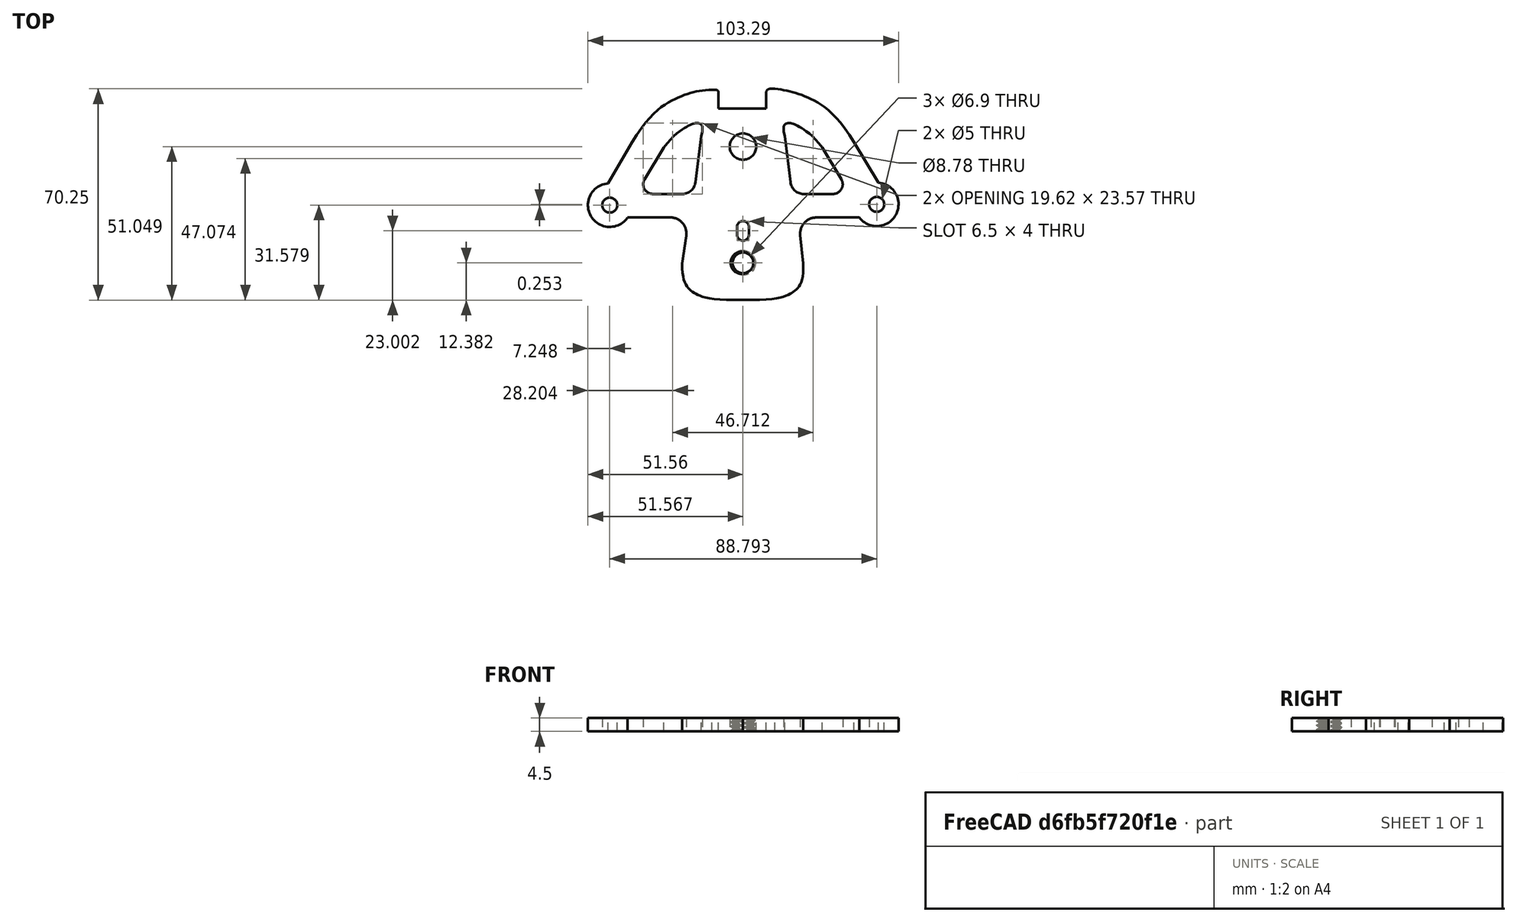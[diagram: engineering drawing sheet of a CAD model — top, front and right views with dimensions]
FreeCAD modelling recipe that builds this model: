
FCSTD DOCUMENT  (FreeCAD 0.20R29603 (Git))
Label: tiller-plate-final-threaded
License: Creative Commons Attribution
LicenseURL: http://creativecommons.org/licenses/by/4.0/
objects: Sketcher::SketchObject×2, Image::ImagePlane×1, PartDesign::Pad×1, PartDesign::Hole×1, PartDesign::Body×1, Part::Refine×1, Mesh::Feature×1
note: 8 computed .brp shape members not serialized (recipe doc carries the construction recipe); baked Part::Feature solids carry a one-line shape summary decoded from their .brp

FEATURE [Image::ImagePlane] ImagePlane
  Placement = pos=(0.718471,-0.887185,-0.1) rot=(0,0,-1;6.26573rad)
  XSize = 116.42
  YSize = 72.9857
FEATURE [Sketcher::SketchObject] Sketch
  FullyConstrained = false
  MapMode = 5
  Support = -> [XY_Plane]
  sketch-geometry (75):
    g0: ArcOfCircle CenterX=-44.3115 CenterY=-4.63128 CenterZ=0 NormalX=0 NormalY=0 NormalZ=1 AngleXU=0 Radius=7.25 StartAngle=1.65486 EndAngle=5.682
    g1: LineSegment StartX=-8.13082 StartY=27.4789 StartZ=0 EndX=7.6791 EndY=27.4789 EndZ=0
    g2: ArcOfCircle CenterX=44.4815 CenterY=-4.37835 CenterZ=0 NormalX=0 NormalY=0 NormalZ=1 AngleXU=0 Radius=7.25 StartAngle=3.79043 EndAngle=7.77353
    g3-g7: Circle x5 (B-spline internal-alignment scaffolding for g8; pole/knot coordinates omitted)
    g8: BSplineCurve PolesCount=5 KnotsCount=3 Degree=3 IsPeriodic=0
    g9: GeomPoint X=-36.8504 Y=16.2655 Z=0
    g10: GeomPoint X=-22.0365 Y=30.9294 Z=0
    g11: GeomPoint X=-10.281 Y=33.7257 Z=0
    g12: LineSegment StartX=-8.13082 StartY=27.4789 StartZ=0 EndX=-8.13082 EndY=32.8031 EndZ=0
    g13: LineSegment StartX=-10.281 StartY=33.7257 StartZ=0 EndX=-9.05342 EndY=33.7257 EndZ=0
    g14: ArcOfCircle CenterX=-9.05342 CenterY=32.8031 CenterZ=0 NormalX=0 NormalY=0 NormalZ=1 AngleXU=0 Radius=0.922601 StartAngle=2.8e-15 EndAngle=1.5708
    g15: LineSegment StartX=-44.9203 StartY=2.59312 StartZ=0 EndX=-36.8504 EndY=16.2655 EndZ=0
    g16: LineSegment StartX=45.0641 StartY=2.84821 StartZ=0 EndX=36.8504 EndY=16.2655 EndZ=0
    g17: BSplineCurve PolesCount=5 KnotsCount=3 Degree=3 IsPeriodic=0
    g18: Circle CenterX=10.5661 CenterY=34.0385 CenterZ=0 NormalX=0 NormalY=0 NormalZ=1 AngleXU=0 Radius=1
    g19: GeomPoint X=10.5661 Y=34.0385 Z=0
    g20: LineSegment StartX=7.6791 StartY=27.4789 StartZ=0 EndX=7.6791 EndY=32.7332 EndZ=0
    g21: LineSegment StartX=10.5661 StartY=34.0385 StartZ=0 EndX=8.9844 EndY=34.0385 EndZ=0
    g22: ArcOfCircle CenterX=8.9844 CenterY=32.7332 CenterZ=0 NormalX=0 NormalY=0 NormalZ=1 AngleXU=0 Radius=1.3053 StartAngle=1.5708 EndAngle=3.14159
    g23: Circle CenterX=0 CenterY=14.839 CenterZ=0 NormalX=0 NormalY=0 NormalZ=1 AngleXU=0 Radius=4.39
    g24: Circle CenterX=-44.3115 CenterY=-4.63128 CenterZ=0 NormalX=0 NormalY=0 NormalZ=1 AngleXU=0 Radius=2.5
    g25: Circle CenterX=44.4815 CenterY=-4.37835 CenterZ=0 NormalX=0 NormalY=0 NormalZ=1 AngleXU=0 Radius=2.5
    g26: Circle CenterX=0 CenterY=-23.8283 CenterZ=0 NormalX=0 NormalY=0 NormalZ=1 AngleXU=0 Radius=3.375
    g27: LineSegment StartX=-24.1418 StartY=-8.73204 StartZ=0 EndX=-38.3327 EndY=-8.73204 EndZ=0
    g28: LineSegment StartX=-18.8831 StartY=-14.7976 StartZ=0 EndX=-20.2109 EndY=-24.0676 EndZ=0
    g29: ArcOfCircle CenterX=-24.1418 CenterY=-14.0444 CenterZ=0 NormalX=0 NormalY=0 NormalZ=1 AngleXU=0 Radius=5.31234 StartAngle=6.14092 EndAngle=7.85398
    g30: LineSegment StartX=24.3717 StartY=-8.75921 StartZ=0 EndX=38.7048 EndY=-8.75921 EndZ=0
    g31: ArcOfCircle CenterX=24.3717 CenterY=-14.1062 CenterZ=0 NormalX=0 NormalY=0 NormalZ=1 AngleXU=0 Radius=5.34701 StartAngle=1.5708 EndAngle=3.24394
    g32: LineSegment StartX=19.0527 StartY=-14.6525 StartZ=0 EndX=20.0104 EndY=-23.9781 EndZ=0
    g33: LineSegment StartX=-1.99308 StartY=-11.9579 StartZ=0 EndX=-1.99308 EndY=-14.4579 EndZ=0
    g34: ArcOfCircle CenterX=0.00691514 CenterY=-14.4579 CenterZ=0 NormalX=0 NormalY=0 NormalZ=1 AngleXU=0 Radius=2 StartAngle=3.14159 EndAngle=6.28319
    g35: LineSegment StartX=2.00692 StartY=-14.4579 StartZ=0 EndX=2.00692 EndY=-11.9579 EndZ=0
    g36: ArcOfCircle CenterX=0.00691514 CenterY=-11.9579 CenterZ=0 NormalX=0 NormalY=0 NormalZ=1 AngleXU=0 Radius=2 StartAngle=0 EndAngle=3.14159
    g37-g41: Circle x5 (B-spline internal-alignment scaffolding for g42; pole/knot coordinates omitted)
    g42: BSplineCurve PolesCount=5 KnotsCount=3 Degree=3 IsPeriodic=0
    g43: GeomPoint X=-20.2109 Y=-24.0676 Z=0
    g44: GeomPoint X=-16.4959 Y=-33.6189 Z=0
    g45: GeomPoint X=0 Y=-36.2033 Z=0
    g46: BSplineCurve PolesCount=5 KnotsCount=3 Degree=3 IsPeriodic=0
    g47: LineSegment StartX=-13.8688 StartY=18.3787 StartZ=0 EndX=-15.7977 EndY=2.95357 EndZ=0
    g48: LineSegment StartX=-29.9555 StartY=-0.921458 StartZ=0 EndX=-20.1874 EndY=-0.921458 EndZ=0
    g49: ArcOfCircle CenterX=-20.1874 CenterY=3.50249 CenterZ=0 NormalX=0 NormalY=0 NormalZ=1 AngleXU=0 Radius=4.42394 StartAngle=4.71239 EndAngle=6.15879
    g50: LineSegment StartX=-26.3153 StartY=14.4759 StartZ=0 EndX=-32.7012 EndY=3.9578 EndZ=0
    g51: ArcOfCircle CenterX=-29.9555 CenterY=2.29074 CenterZ=0 NormalX=0 NormalY=0 NormalZ=1 AngleXU=0 Radius=3.2122 StartAngle=2.59594 EndAngle=4.71239
    g52-g57: Circle x6 (B-spline internal-alignment scaffolding for g58; pole/knot coordinates omitted)
    g58: BSplineCurve PolesCount=6 KnotsCount=4 Degree=3 IsPeriodic=0
    g59-g62: GeomPoint x4 (B-spline internal-alignment scaffolding for g58; pole/knot coordinates omitted)
    g63: GeomPoint X=0 Y=-23.8283 Z=0
    g64: LineSegment StartX=26.3153 StartY=14.4759 StartZ=0 EndX=32.7012 EndY=3.9578 EndZ=0
    g65: BSplineCurve PolesCount=6 KnotsCount=4 Degree=3 IsPeriodic=0
    g66: LineSegment StartX=13.8688 StartY=18.3787 StartZ=0 EndX=15.7977 EndY=2.95357 EndZ=0
    g67: ArcOfCircle CenterX=20.1874 CenterY=3.50249 CenterZ=0 NormalX=0 NormalY=0 NormalZ=1 AngleXU=0 Radius=4.42394 StartAngle=3.26599 EndAngle=4.71239
    g68: LineSegment StartX=29.9555 StartY=-0.921458 StartZ=0 EndX=20.1874 EndY=-0.921458 EndZ=0
    g69: ArcOfCircle CenterX=29.9555 CenterY=2.29074 CenterZ=0 NormalX=0 NormalY=0 NormalZ=1 AngleXU=0 Radius=3.2122 StartAngle=4.71239 EndAngle=6.82884
    g70: GeomPoint X=-0.103427 Y=-16.4548 Z=0
    g71: GeomPoint X=-0.101997 Y=-20.4548 Z=0
    g72: GeomPoint X=0.0131789 Y=-27.2033 Z=0
    g73: GeomPoint X=-0.00257 Y=27.4789 Z=0
    g74: GeomPoint X=-0.0300529 Y=19.2289 Z=0
  constraints (86):
    c: Radius(g0) = 7.25
    c: Horizontal(g1)
    c: Equal(g2,g0)
    c: Equal(g3, g4-g7) x4
    c: InternalAlignment(g3-g7 -> g8) x5
    c: InternalAlignment(g9,g8)
    c: InternalAlignment(g10,g8)
    c: InternalAlignment(g11,g8)
    c: Coincident(g12,g1)
    c: Coincident(g13,g8)
    c: Horizontal(g13)
    c: Tangent(g12,g14) = -1.5708
    c: Tangent(g13,g14) = 1.5708
    c: Coincident(g15,g8)
    c: InternalAlignment(g18,g17)
    c: InternalAlignment(g19,g17)
    c: Coincident(g21,g17)
    c: Horizontal(g21)
    c: Tangent(g20,g22) = 1.5708
    c: Tangent(g21,g22) = -1.5708
    c: Coincident(g16,g17)
    c: PointOnObject(g23,g-2)
    c: Coincident(g24,g0)
    c: Diameter(g24) = 5
    c: Diameter(g25) = 5
    c: PointOnObject(g26,g-2)
    c: Horizontal(g27)
    c: Tangent(g27,g29) = -1.5708
    c: Tangent(g28,g29) = 1.5708
    c: Horizontal(g30)
    c: Tangent(g30,g31) = 1.5708
    c: Tangent(g32,g31) = -1.5708
    c: Coincident(g2,g25)
    c: Vertical(g33)
    c: Tangent(g33,g34) = -1.5708
    c: Tangent(g34,g35) = -1.5708
    c: Tangent(g35,g36) = -1.5708
    c: Radius(g36) = 2
    c: Equal(g34,g36)
    c: DistanceY(g34,g36) = 2.5
    c: Vertical(g35)
    c: Coincident(g33,g36)
    c: Equal(g37, g38-g41) x4
    c: PointOnObject(g42,g-2)
    c: InternalAlignment(g37-g41 -> g42) x5
    c: InternalAlignment(g43,g42)
    c: InternalAlignment(g44,g42)
    c: InternalAlignment(g45,g42)
    c: Coincident(g28,g42)
    c: Horizontal(g48)
    c: Tangent(g47,g49) = 1.5708
    c: Tangent(g48,g49) = -1.5708
    c: Tangent(g48,g51) = -1.5708
    c: Tangent(g50,g51) = -1.5708
    c: Coincident(g58,g50)
    c: Equal(g52, g53-g57) x5
    c: Coincident(g58,g47)
    c: InternalAlignment(g52-g57 -> g58) x6
    c: InternalAlignment(g59-g62 -> g58) x4
    c: Coincident(g63,g26)
    c: Horizontal(g68)
    c: Tangent(g66,g67) = -1.5708
    c: Tangent(g68,g67) = 1.5708
    c: Tangent(g68,g69) = 1.5708
    c: Tangent(g64,g69) = 1.5708
    c: Coincident(g65,g64)
    c: Coincident(g65,g66)
    c: Coincident(g0,g27)
    c: Coincident(g0,g15)
    c: Coincident(g2,g16)
    c: Coincident(g2,g30)
    c: Coincident(g46,g42)
    c: Vertical(g20)
    c: Vertical(g12)
    c: Coincident(g20,g1)
    c: Coincident(g32,g46)
    c: PointOnObject(g70,g34)
    c: PointOnObject(g71,g26)
    c: DistanceY(g71,g70) = 4
    c: PointOnObject(g72,g26)
    c: DistanceY(g42,g72) = 9
    c: PointOnObject(g73,g1)
    c: PointOnObject(g74,g23)
    c: DistanceY(g74,g73) = 8.25
    c: Diameter(g26) = 6.75
    c: Diameter(g23) = 8.78
FEATURE [PartDesign::Pad] Pad  label="Pad-tiller-plate"
  Direction = (0,0,1)
  Length = 4.5
  Length2 = 10
  Profile = -> Sketch
  ReferenceAxis = -> Sketch [N_Axis]
  Refine = true
  Type = 0
FEATURE [Sketcher::SketchObject] Sketch002  label="Sketch-threaded-hole001"
  ExternalGeometry = -> [Pad]
  FullyConstrained = true
  MapMode = 5
  Placement = pos=(0,0,4.5) rot=(0,0,1;0rad)
  Support = -> [Pad]
  sketch-geometry (1):
    g0: Circle CenterX=0 CenterY=-23.8283 CenterZ=0 NormalX=0 NormalY=0 NormalZ=1 AngleXU=0 Radius=3.375
  constraints (2):
    c: Coincident(g0,g-3)
    c: Equal(g0,g-3)
FEATURE [PartDesign::Hole] Hole  label="Hole - tillerPlate with 5/16 threaded UNC"
  BaseFeature = -> Pad
  CustomThreadClearance = 0.3
  Depth = 25
  DepthType = 0
  Diameter = 6.9
  DrillForDepth = false
  DrillPoint = 1
  DrillPointAngle = 118
  HoleCutCountersinkAngle = 90
  HoleCutCustomValues = false
  HoleCutDepth = 0
  HoleCutDiameter = 6.1
  HoleCutType = 0
  ModelThread = true
  Profile = -> Sketch002
  Refine = true
  Tapered = false
  TaperedAngle = 90
  ThreadClass = 0
  ThreadDepth = 25
  ThreadDepthType = 0
  ThreadDirection = 0
  ThreadFit = 0
  ThreadSize = 10
  ThreadType = 3
  Threaded = true
  UseCustomThreadClearance = true
FEATURE [PartDesign::Body] Body  label="Body-tiller-plate"
  Group = -> [Sketch,Pad,Sketch002,Hole]
  Origin = -> Origin
  Tip = -> Hole
FEATURE [Part::Refine] Hole001  label="refined_tillerPlate-with-5/16-UNC-threads"
  Source = -> Hole
FEATURE [Mesh::Feature] Mesh  label="refined_tillerPlate-with-5/16-UNC-threads (Meshed)"
